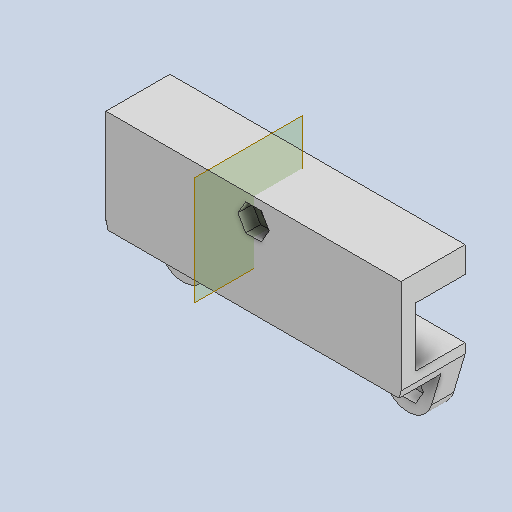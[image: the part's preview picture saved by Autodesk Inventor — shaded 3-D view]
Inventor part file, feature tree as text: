
AUTODESK INVENTOR PART (.ipt)
format: ipt  version: 2023 (Build 270158000, 158)  size: 521,216 bytes
history: native  units: in
note: dims shown in document units (in); Inventor stores cm internally (conversion verified against a paired STEP export)
features: extrude x14, sketch x14, other x12, reference x8, projected_geometry x6, fillet x3, mirror x1
ambient origin geometry x8: Origin, YZ Plane, XZ Plane, XY Plane, X Axis, Y Axis, Z Axis, Center Point
bodies: Solid2 (feature_tree)
feature tree (58):
  other  "Bryła1"
  extrude  "Wyciągnięcie proste1"  TaperAngle=0.0deg  [1 undecoded]
  extrude  "Wyciągnięcie proste2"  Depth=0.2559in
  extrude  "Wyciągnięcie proste3"  Depth=0.1181in
  extrude  "Wyciągnięcie proste4"  Depth=0.2165in
  extrude  "Wyciągnięcie proste5"  Depth=0.3937in
  extrude  "Wyciągnięcie proste6"  Depth=0.1772in TaperAngle=0.0deg
  extrude  "Wyciągnięcie proste7"  Depth=0.0591in
  extrude  "Wyciągnięcie proste8"  Depth=0.1772in TaperAngle=0.0deg
  extrude  "Wyciągnięcie proste9"  Depth=0.3937in TaperAngle=0.0deg
  fillet  "Zaokrąglenie1"  Radius=0.0787in
  other  "Edytuj bezpośrednio1"
  other  "Edytuj bezpośrednio2"
  extrude  "Wyciągnięcie proste10"  Depth=0.1181in
  other  "Edytuj bezpośrednio3"
  extrude  "Wyciągnięcie proste11"  Depth=0.0748in TaperAngle=0.0deg
  other  "Płaszczyzna konstrukcyjna1"
  mirror  "Odbij1"
  extrude  "Wyciągnięcie proste12"  Depth=0.1181in
  fillet  "Zaokrąglenie2"  Radius=0.1181in
  extrude  "Wyciągnięcie proste13"  Depth=0.0787in
  fillet  "Zaokrąglenie3"  Radius=0.2165in
  extrude  "Wyciągnięcie proste14"  Depth=0.0787in
  sketch  "Szkic1"
  projected_geometry  "Pętla rzutowana1"
  reference  "Odniesienie1"
  sketch  "Szkic2"
  reference  "Odniesienie2"
  sketch  "Szkic3"
  projected_geometry  "Pętla rzutowana2"
  sketch  "Szkic4"
  reference  "Odniesienie3"
  sketch  "Szkic5"
  projected_geometry  "Pętla rzutowana3"
  sketch  "Szkic6"
  reference  "Odniesienie4"
  sketch  "Szkic7"
  reference  "Odniesienie5"
  reference  "Odniesienie6"
  reference  "Odniesienie7"
  sketch  "Szkic8"
  sketch  "Szkic9"
  projected_geometry  "Pętla rzutowana4"
  sketch  "Szkic10"
  projected_geometry  "Pętla rzutowana5"
  sketch  "Szkic11"
  sketch  "Szkic12"
  sketch  "Szkic13"
  reference  "Odniesienie8"
  sketch  "Szkic14"
  projected_geometry  "Pętla rzutowana6"
  other  "Zespół3"
  other  "minisumopodsr:1"
  other  "n20 motor:2"
  other  "n20 motor:1"
  other  "Przesuń1"
  other  "Przesuń2"
  other  "Przesuń3"
note: 1 required parameter value undecoded (feature->parameter linkage not recoverable at this tier; creation-order binding heuristic only, values carry confidence <= 0.55)
